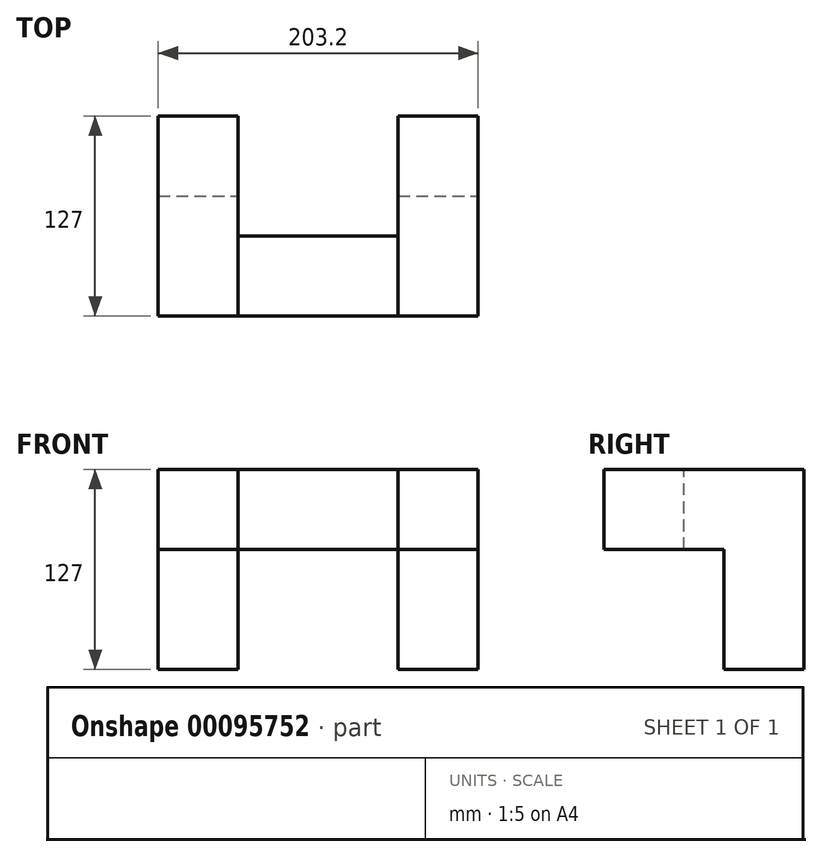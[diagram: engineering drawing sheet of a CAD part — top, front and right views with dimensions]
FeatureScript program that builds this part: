
annotation { "Feature Type Name" : "Feature", "Feature Type Description" : "" }
export const myFeature = defineFeature(function(context is Context, id is Id, definition is map)
    precondition{}
    {
        {
            var Q0;
            Q0=qCreatedBy(makeId("Front.planeOp"),FACE);
            var sketch = newSketch(context, id + "F0", { "sketchPlane" : qUnion([Q0])});
            skLineSegment(sketch, "E0", {"start": v(-101.07, 42.48) * mm, "end": v(-101.07, -84.52) * mm});
            skLineSegment(sketch, "E1", {"start": v(-101.07, -84.52) * mm, "end": v(-50.27, -84.52) * mm});
            skLineSegment(sketch, "E2", {"start": v(-101.07, 42.48) * mm, "end": v(-50.27, 42.48) * mm});
            skLineSegment(sketch, "E3", {"start": v(-50.27, 42.48) * mm, "end": v(-50.27, -84.52) * mm});
            skLineSegment(sketch, "E4", {"start": v(51.33, 42.48) * mm, "end": v(51.33, -84.52) * mm});
            skLineSegment(sketch, "E5", {"start": v(51.33, -84.52) * mm, "end": v(102.13, -84.52) * mm});
            skLineSegment(sketch, "E6", {"start": v(102.13, -84.52) * mm, "end": v(102.13, 42.48) * mm});
            skLineSegment(sketch, "E7", {"start": v(102.13, 42.48) * mm, "end": v(51.33, 42.48) * mm});
            skSolve(sketch);
        }
        {
            var Q0;
            Q0 = qSketchRegion(id + "F0", true);
            extrude(context, id + "F1", {"entities" : qUnion([Q0]), "depth" : 50.8 * mm});
        }
        {
            var Q0;
            Q0=makeQuery(id+"F1.opExtrude","CAP_FACE",FACE,{"disambiguationData":[OSD([sQuery(id+"F0.wireOp",EDGE,"E4"),sQuery(id+"F0.wireOp",EDGE,"E5"),sQuery(id+"F0.wireOp",EDGE,"E6"),sQuery(id+"F0.wireOp",EDGE,"E7")])],"isStart":false});
            var sketch = newSketch(context, id + "F2", { "sketchPlane" : qUnion([Q0])});
            skLineSegment(sketch, "E8.bottom", {"start": v(51.33, 42.48) * mm, "end": v(102.13, 42.48) * mm});
            skLineSegment(sketch, "E8.top", {"start": v(51.33, -8.32) * mm, "end": v(102.13, -8.32) * mm});
            skLineSegment(sketch, "E8.left", {"start": v(51.33, 42.48) * mm, "end": v(51.33, -8.32) * mm});
            skLineSegment(sketch, "E8.right", {"start": v(102.13, 42.48) * mm, "end": v(102.13, -8.32) * mm});
            skSolve(sketch);
        }
        {
            var Q0;
            Q0 = qSketchRegion(id + "F2", true);
            extrude(context, id + "F3", {"entities" : qUnion([Q0]), "operationType" : NewBodyOperationType.ADD, "depth" : 76.2 * mm});
        }
        {
            var Q0;
            Q0=makeQuery(id+"F1.opExtrude","CAP_FACE",FACE,{"disambiguationData":[OSD([sQuery(id+"F0.wireOp",EDGE,"E0"),sQuery(id+"F0.wireOp",EDGE,"E1"),sQuery(id+"F0.wireOp",EDGE,"E2"),sQuery(id+"F0.wireOp",EDGE,"E3")])],"isStart":false});
            var sketch = newSketch(context, id + "F4", { "sketchPlane" : qUnion([Q0])});
            skLineSegment(sketch, "E9.bottom", {"start": v(-101.07, 42.48) * mm, "end": v(-50.27, 42.48) * mm});
            skLineSegment(sketch, "E9.top", {"start": v(-101.07, -8.32) * mm, "end": v(-50.27, -8.32) * mm});
            skLineSegment(sketch, "E9.left", {"start": v(-101.07, 42.48) * mm, "end": v(-101.07, -8.32) * mm});
            skLineSegment(sketch, "E9.right", {"start": v(-50.27, 42.48) * mm, "end": v(-50.27, -8.32) * mm});
            skSolve(sketch);
        }
        {
            var Q0;
            Q0 = qSketchRegion(id + "F4", true);
            extrude(context, id + "F5", {"entities" : qUnion([Q0]), "operationType" : NewBodyOperationType.ADD, "depth" : 76.2 * mm});
        }
        {
            var Q0;
            Q0=makeQuery(id+"F5.boolean.opBoolean","MERGE",FACE,{"derivedFrom":[makeQuery(id+"F1.opExtrude","SWEPT_FACE",FACE,{"disambiguationData":[OSD([sQuery(id+"F0.wireOp",EDGE,"E3")])]}),makeQuery(id+"F5.opExtrude","SWEPT_FACE",FACE,{"disambiguationData":[OSD([sQuery(id+"F4.wireOp",EDGE,"E9.right")])]})]});
            var sketch = newSketch(context, id + "F6", { "sketchPlane" : qUnion([Q0])});
            skLineSegment(sketch, "E10.bottom", {"start": v(-127, -8.32) * mm, "end": v(-76.2, -8.32) * mm});
            skLineSegment(sketch, "E10.top", {"start": v(-127, 42.48) * mm, "end": v(-76.2, 42.48) * mm});
            skLineSegment(sketch, "E10.left", {"start": v(-127, -8.32) * mm, "end": v(-127, 42.48) * mm});
            skLineSegment(sketch, "E10.right", {"start": v(-76.2, -8.32) * mm, "end": v(-76.2, 42.48) * mm});
            skSolve(sketch);
        }
        {
            var Q0;
            Q0 = qSketchRegion(id + "F6", true);
            extrude(context, id + "F7", {"entities" : qUnion([Q0]), "depth" : 101.6 * mm});
        }
    });
